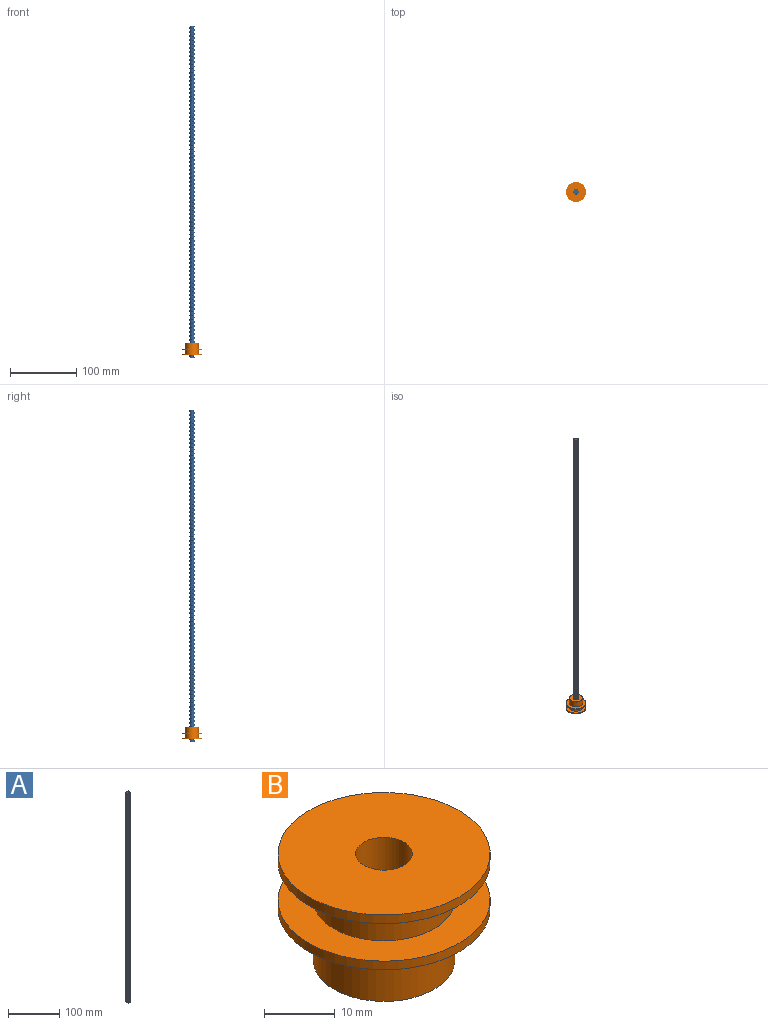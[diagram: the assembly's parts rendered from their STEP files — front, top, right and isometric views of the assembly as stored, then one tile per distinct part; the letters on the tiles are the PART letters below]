
ASSEMBLY  parts=2 mates=1
PART A: 8 faces, bbox 8x9.2x500.6 mm
  f0: cylinder r=4mm len=500mm, axis (0,0,-1), area 11503.3mm2, adj f1,f2,f3,f5,f6,f7
  f1: plane 8x7.69mm, normal (0,0,1), area 44.7mm2, adj f0,f4,f6,f7
  f2: plane 8x7.69mm, normal (0,0,-1), area 44.7mm2, adj f0,f3,f4,f5
  f3: plane 1x0.64mm, normal (0,1,0), area 0.5mm2, adj f0,f2,f4,f7
  f4: cylinder r=3mm len=500mm, axis (0,0,-1), area -4898.1mm2, adj f1,f2,f3,f5,f6,f7
  f5: bspline ~499.94x9.24mm, area 5685.1mm2, adj f0,f2,f4,f6
  f6: plane 1x0.64mm, normal (0,-1,0), area 0.5mm2, adj f0,f1,f4,f5
  f7: bspline ~500.27x9.24mm, area 5687.7mm2, adj f0,f1,f3,f4
PART B: 11 faces, bbox 30x30x18.5 mm
  f0: cylinder r=4.01mm len=18.5mm, axis (0,0,-1), area 463mm2, adj f2,f8,f10
  f1: cylinder r=10mm len=20mm, axis (0,0,-1), area 562.3mm2, adj f2,f5,f10
  f2: plane 20x20mm, normal (0,0,-1), area 263.6mm2, adj f0,f1
  f3: cylinder r=15mm len=30mm, axis (0,0,-1), area 141.4mm2, adj f4,f5
  f4: plane 30x30mm, normal (0,0,1), area 392.7mm2, adj f3,f6
  f5: plane 30x30mm, normal (0,0,-1), area 392.7mm2, adj f1,f3
  f6: cylinder r=10mm len=20mm, axis (0,0,-1), area 408.4mm2, adj f4,f9
  f7: cylinder r=15mm len=30mm, axis (0,0,-1), area 141.4mm2, adj f8,f9
  f8: plane 30x30mm, normal (0,0,1), area 656.3mm2, adj f0,f7
  f9: plane 30x30mm, normal (0,0,-1), area 392.7mm2, adj f6,f7
  f10: cylinder r=1mm len=6.12mm, axis (-1,0,0), area 37.9mm2, adj f0,f1
PLACE A t=(-126.6,39.41,-81.25)mm
PLACE B rot(axis=(1,0,0),180deg) t=(-126.6,39.41,-58.25)mm
MATE fastened B.f1 <-> A.f0  axis (0,0,1) through (-126.6,39.41,-58.25)mm
